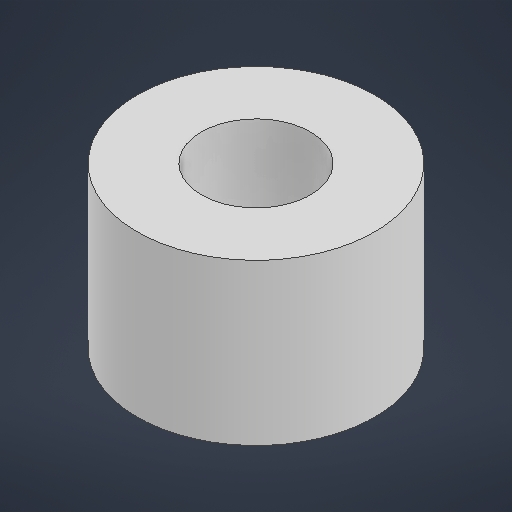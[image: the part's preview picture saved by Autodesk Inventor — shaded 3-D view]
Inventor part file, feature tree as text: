
AUTODESK INVENTOR PART (.ipt)
format: ipt  version: 2025 (Build 290162000, 162)  size: 161,280 bytes
history: native  units: mm
features: extrude x1, sketch x1
ambient origin geometry x8: Origin, YZ Plane, XZ Plane, XY Plane, X Axis, Y Axis, Z Axis, Center Point
bodies: Solid1 (feature_tree)
feature tree (2):
  extrude  "Extrusion1"  Depth=5.0mm
  sketch  "Sketch1"  dims[d0=3.4mm d1=2.0mm d2=5.0mm d3=0.0mm]
